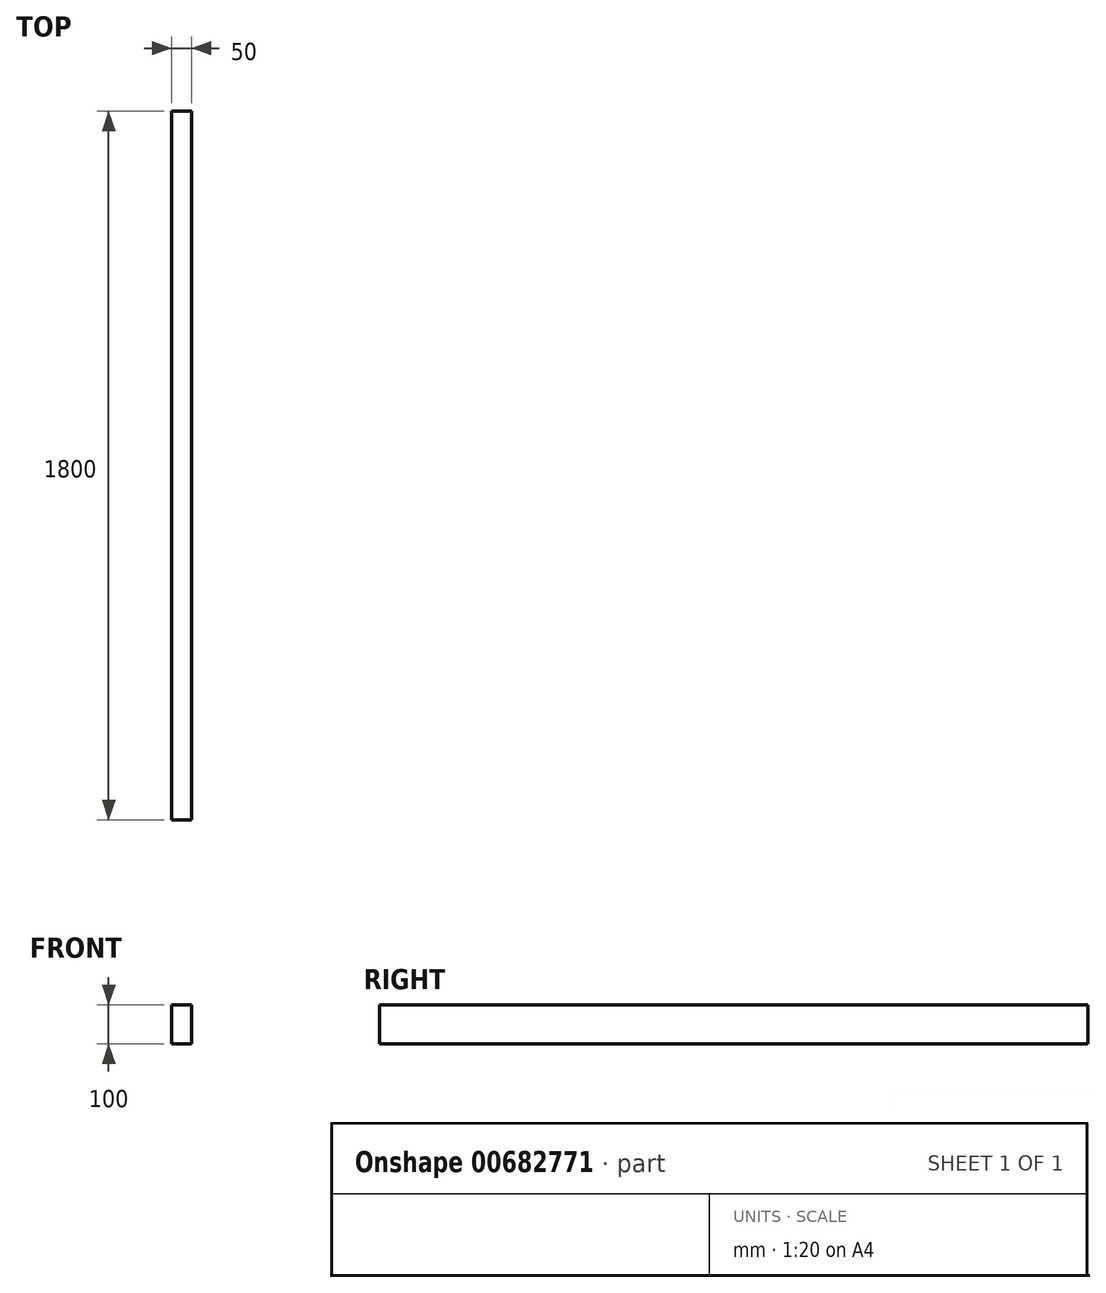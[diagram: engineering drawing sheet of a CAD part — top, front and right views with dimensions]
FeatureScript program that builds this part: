
annotation { "Feature Type Name" : "Feature", "Feature Type Description" : "" }
export const myFeature = defineFeature(function(context is Context, id is Id, definition is map)
    precondition{}
    {
        {
            var Q0;
            Q0=qCreatedBy(makeId("Front.planeOp"),FACE);
            var sketch = newSketch(context, id + "F0", { "sketchPlane" : qUnion([Q0])});
            skLineSegment(sketch, "E0.bottom", {"start": v(-85.58, 116.4) * mm, "end": v(-35.58, 116.4) * mm});
            skLineSegment(sketch, "E0.top", {"start": v(-85.58, 16.4) * mm, "end": v(-35.58, 16.4) * mm});
            skLineSegment(sketch, "E0.left", {"start": v(-85.58, 116.4) * mm, "end": v(-85.58, 16.4) * mm});
            skLineSegment(sketch, "E0.right", {"start": v(-35.58, 116.4) * mm, "end": v(-35.58, 16.4) * mm});
            skSolve(sketch);
        }
        {
            var Q0;
            Q0=qSketchRegion(id+"F0",true);
            extrude(context, id + "F1", {"entities" : qUnion([Q0]), "depth" : 1800 * mm, "offsetDistance" : 25 * mm});
        }
    });
